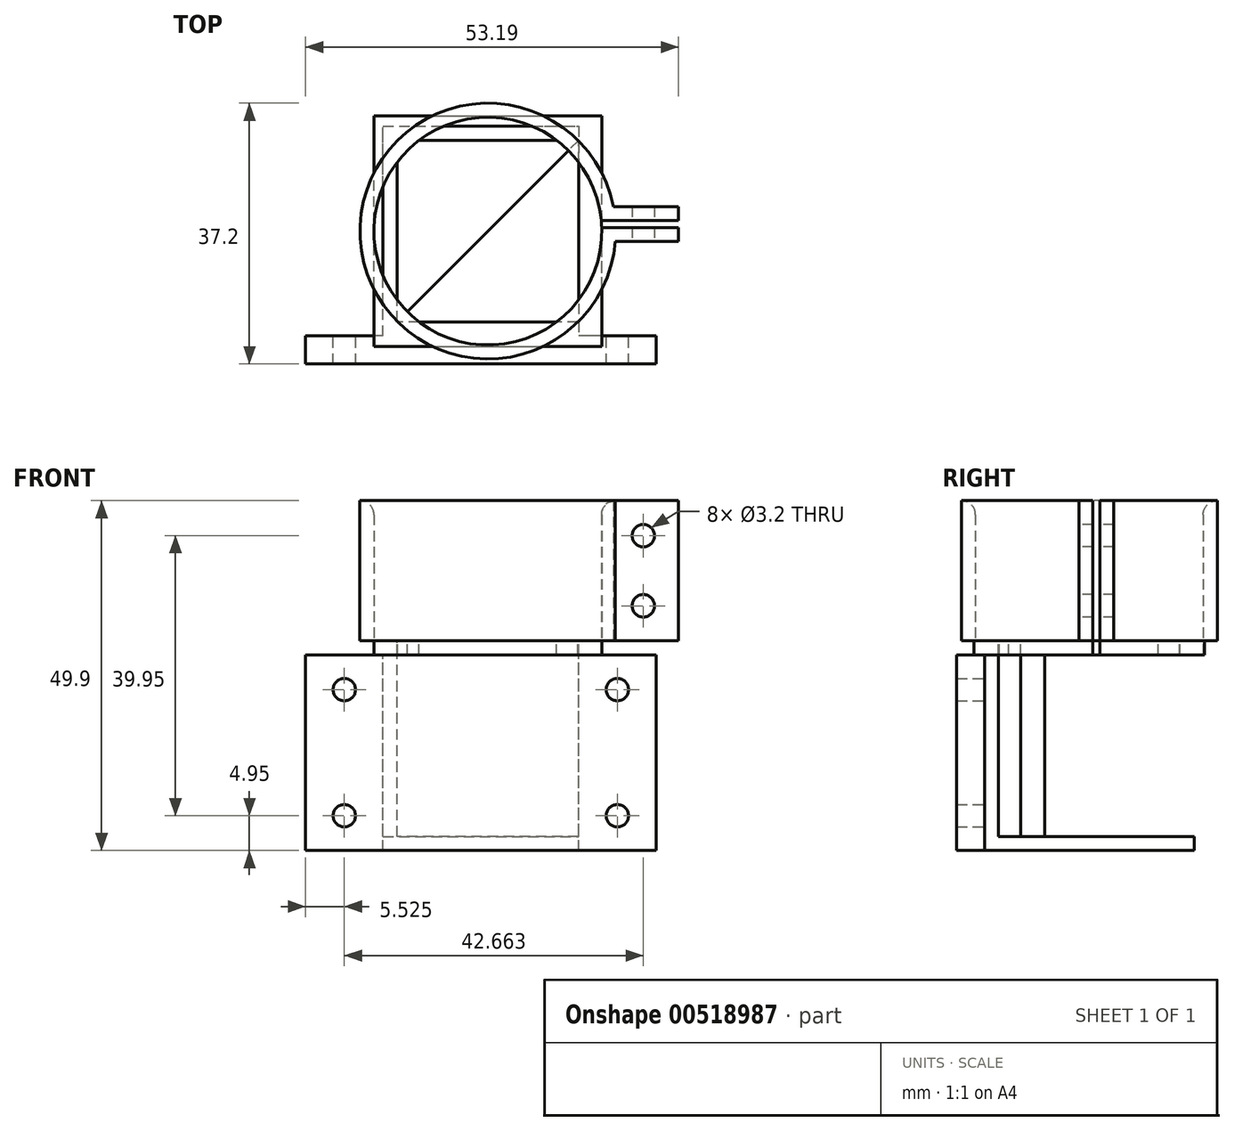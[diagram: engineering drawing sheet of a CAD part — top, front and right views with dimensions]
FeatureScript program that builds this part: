
annotation { "Feature Type Name" : "Feature", "Feature Type Description" : "" }
export const myFeature = defineFeature(function(context is Context, id is Id, definition is map)
    precondition{}
    {
        {
            var Q0;
            Q0=qCreatedBy(makeId("Top.planeOp"),FACE);
            var sketch = newSketch(context, id + "F0", { "sketchPlane" : qUnion([Q0])});
            skCircle(sketch, "E0", {"center": v(0, 0) * mm, "radius": 16.25 * mm});
            skCircle(sketch, "E1", {"center": v(0, 0) * mm, "radius": 18.25 * mm});
            skLineSegment(sketch, "E2", {"start": v(16.18, 1.5) * mm, "end": v(18.19, 1.5) * mm});
            skLineSegment(sketch, "E3", {"start": v(16.24, 0.5) * mm, "end": v(18.19, 0.5) * mm});
            skLineSegment(sketch, "E4", {"start": v(17.91, 3.5) * mm, "end": v(27.19, 3.5) * mm});
            skLineSegment(sketch, "E5", {"start": v(27.19, 3.5) * mm, "end": v(27.19, 1.5) * mm});
            skLineSegment(sketch, "E6", {"start": v(27.19, 1.5) * mm, "end": v(18.19, 1.5) * mm});
            skLineSegment(sketch, "E7", {"start": v(18.19, 0.5) * mm, "end": v(27.19, 0.5) * mm});
            skLineSegment(sketch, "E8", {"start": v(27.19, 0.5) * mm, "end": v(27.19, -1.5) * mm});
            skLineSegment(sketch, "E9", {"start": v(27.19, -1.5) * mm, "end": v(18.19, -1.5) * mm});
            skSolve(sketch);
        }
        {
            var Q0;
            {var subQ0=sQuery(id+"F0.wireOp",EDGE,"E2");Q0=makeQuery(id+"F0.imprint","IMPRINT",FACE,{"disambiguationData":[TD([[makeQuery(id+"F0.imprint","IMPRINT",EDGE,{"derivedFrom":subQ0}),1.0]])]});}
            var Q1;
            {var subQ2=sQuery(id+"F0.wireOp",EDGE,"E4");Q1=makeQuery(id+"F0.imprint","IMPRINT",FACE,{"disambiguationData":[TD([[makeQuery(id+"F0.imprint","IMPRINT",EDGE,{"derivedFrom":subQ2}),-1.0]])]});}
            var Q2;
            {var subQ4=sQuery(id+"F0.wireOp",EDGE,"E8");Q2=makeQuery(id+"F0.imprint","IMPRINT",FACE,{"disambiguationData":[TD([[makeQuery(id+"F0.imprint","IMPRINT",EDGE,{"derivedFrom":subQ4}),-1.0]])]});}
            extrude(context, id + "F1", {"entities" : qUnion([Q0, Q1, Q2]), "depth" : 20 * mm, "offsetDistance" : 25 * mm});
        }
        {
            var Q0;
            Q0=makeQuery(id+"F1.opExtrude","SWEPT_FACE",FACE,{"disambiguationData":[OSD([sQuery(id+"F0.wireOp",EDGE,"E9")])]});
            var sketch = newSketch(context, id + "F2", { "sketchPlane" : qUnion([Q0])});
            skCircle(sketch, "E10", {"center": v(22.19, 15) * mm, "radius": 1.6 * mm});
            skCircle(sketch, "E11", {"center": v(22.19, 5) * mm, "radius": 1.6 * mm});
            skLineSegment(sketch, "E12", {"start": v(22.19, 15) * mm, "end": v(22.19, 20) * mm, "construction": true});
            skLineSegment(sketch, "E13", {"start": v(22.19, 5) * mm, "end": v(22.19, 0) * mm, "construction": true});
            skLineSegment(sketch, "E14", {"start": v(22.19, 15) * mm, "end": v(22.19, 10) * mm, "construction": true});
            skLineSegment(sketch, "E15", {"start": v(22.19, 10) * mm, "end": v(22.19, 5) * mm, "construction": true});
            skLineSegment(sketch, "E16", {"start": v(22.19, 5) * mm, "end": v(27.19, 5) * mm, "construction": true});
            skSolve(sketch);
        }
        {
            var Q0;
            Q0=qSketchRegion(id+"F2",true);
            extrude(context, id + "F3", {"entities" : qUnion([Q0]), "operationType" : NewBodyOperationType.REMOVE, "oppositeDirection" : true, "depth" : 25 * mm, "offsetDistance" : 25 * mm});
        }
        {
            var Q0;
            Q0=makeQuery(id+"F1.opExtrude","CAP_EDGE",EDGE,{"disambiguationData":[OSD([sQuery(id+"F0.wireOp",EDGE,"E0")])],"isStart":false});
            fillet(context, id + "F4", {"entities" : qUnion([Q0]), "radius" : 2 * mm, "tangentPropagation" : true, "allowEdgeOverflow" : false});
        }
        {
            assignVariable(context, id + "F5", {"name" : "PrismSize", "anyValue" : 25.9 * mm});
        }
        {
            var Q0;
            {var subQ5=sQuery(id+"F0.wireOp",EDGE,"E2");Q0=makeQuery(id+"F0.imprint","IMPRINT",FACE,{"disambiguationData":[TD([[makeQuery(id+"F0.imprint","IMPRINT",EDGE,{"derivedFrom":subQ5}),1.0]])]});}
            var sketch = newSketch(context, id + "F6", { "sketchPlane" : qUnion([Q0])});
            skCircle(sketch, "E17", {"center": v(0, 0) * mm, "radius": 16.25 * mm});
            skLineSegment(sketch, "E18.bottom", {"start": v(-12.95, -12.95) * mm, "end": v(12.95, -12.95) * mm});
            skLineSegment(sketch, "E18.top", {"start": v(-12.95, 12.95) * mm, "end": v(12.95, 12.95) * mm});
            skLineSegment(sketch, "E18.left", {"start": v(-12.95, -12.95) * mm, "end": v(-12.95, 12.95) * mm});
            skLineSegment(sketch, "E18.right", {"start": v(12.95, -12.95) * mm, "end": v(12.95, 12.95) * mm});
            skLineSegment(sketch, "E19.bottom", {"start": v(-16.26, -16.45) * mm, "end": v(16.26, -16.45) * mm});
            skLineSegment(sketch, "E19.top", {"start": v(-16.26, 16.45) * mm, "end": v(16.26, 16.45) * mm});
            skLineSegment(sketch, "E19.left", {"start": v(-16.26, -16.45) * mm, "end": v(-16.26, 16.45) * mm});
            skLineSegment(sketch, "E19.right", {"start": v(16.26, -16.45) * mm, "end": v(16.26, 16.45) * mm});
            skLineSegment(sketch, "E20", {"start": v(12.95, 12.95) * mm, "end": v(-12.95, -12.95) * mm});
            skLineSegment(sketch, "E21", {"start": v(12.95, -12.95) * mm, "end": v(-12.95, 12.95) * mm});
            skSolve(sketch);
        }
        {
            var Q0;
            {var subQ0=sQuery(id+"F6.wireOp",EDGE,"E19.left");var subQ1=sQuery(id+"F6.wireOp",EDGE,"E19.bottom");var subQ2=makeQuery(id+"F6.imprint","INTERSECT",VERTEX,{"derivedFrom":[subQ1,subQ0]});Q0=makeQuery(id+"F6.imprint","IMPRINT",FACE,{"disambiguationData":[TD([[makeQuery(id+"F6.imprint","IMPRINT",EDGE,{"disambiguationData":[TD([[subQ2,-1.0]])],"derivedFrom":subQ1}),1.0]])]});}
            var Q1;
            {var subQ6=sQuery(id+"F6.wireOp",EDGE,"E17");var subQ7=makeQuery(id+"F0.imprint","IMPRINT",EDGE,{"derivedFrom":sQuery(id+"F0.wireOp",EDGE,"E2")});var subQ8=makeQuery(id+"F6.imprint","INTERSECT",VERTEX,{"derivedFrom":[subQ7,subQ6]});Q1=makeQuery(id+"F6.imprint","IMPRINT",FACE,{"disambiguationData":[TD([[makeQuery(id+"F6.imprint","IMPRINT",EDGE,{"disambiguationData":[TD([[subQ8,-1.0]])],"derivedFrom":subQ6}),-1.0]])]});}
            var Q2;
            {var subQ0=sQuery(id+"F6.wireOp",EDGE,"E18.top");var subQ1=sQuery(id+"F6.wireOp",EDGE,"E17");var subQ2=makeQuery(id+"F6.imprint","INTERSECT",VERTEX,{"disambiguationData":[OD(0.0)],"derivedFrom":[subQ1,subQ0]});Q2=makeQuery(id+"F6.imprint","IMPRINT",FACE,{"disambiguationData":[TD([[makeQuery(id+"F6.imprint","IMPRINT",EDGE,{"disambiguationData":[TD([[subQ2,-1.0]])],"derivedFrom":subQ1}),1.0]])]});}
            var Q3;
            {var subQ0=sQuery(id+"F6.wireOp",EDGE,"E19.left");var subQ1=sQuery(id+"F6.wireOp",EDGE,"E19.top");var subQ2=makeQuery(id+"F6.imprint","INTERSECT",VERTEX,{"derivedFrom":[subQ1,subQ0]});Q3=makeQuery(id+"F6.imprint","IMPRINT",FACE,{"disambiguationData":[TD([[makeQuery(id+"F6.imprint","IMPRINT",EDGE,{"disambiguationData":[TD([[subQ2,-1.0]])],"derivedFrom":subQ1}),-1.0]])]});}
            var Q4;
            {var subQ0=sQuery(id+"F6.wireOp",EDGE,"E17");var subQ1=makeQuery(id+"F6.imprint","INTERSECT",VERTEX,{"derivedFrom":[makeQuery(id+"F0.imprint","IMPRINT",EDGE,{"derivedFrom":sQuery(id+"F0.wireOp",EDGE,"E2")}),subQ0]});Q4=makeQuery(id+"F6.imprint","IMPRINT",FACE,{"disambiguationData":[TD([[makeQuery(id+"F6.imprint","IMPRINT",EDGE,{"disambiguationData":[TD([[subQ1,1.0]])],"derivedFrom":subQ0}),1.0]])]});}
            var Q5;
            {var subQ0=sQuery(id+"F6.wireOp",EDGE,"E18.left");var subQ1=sQuery(id+"F6.wireOp",EDGE,"E17");var subQ2=makeQuery(id+"F6.imprint","INTERSECT",VERTEX,{"disambiguationData":[OD(0.0)],"derivedFrom":[subQ1,subQ0]});Q5=makeQuery(id+"F6.imprint","IMPRINT",FACE,{"disambiguationData":[TD([[makeQuery(id+"F6.imprint","IMPRINT",EDGE,{"disambiguationData":[TD([[subQ2,-1.0]])],"derivedFrom":subQ1}),1.0]])]});}
            var Q6;
            {var subQ5=sQuery(id+"F6.wireOp",EDGE,"E18.left");var subQ6=sQuery(id+"F6.wireOp",EDGE,"E17");var subQ7=makeQuery(id+"F6.imprint","INTERSECT",VERTEX,{"disambiguationData":[OD(0.0)],"derivedFrom":[subQ6,subQ5]});Q6=makeQuery(id+"F6.imprint","IMPRINT",FACE,{"disambiguationData":[TD([[makeQuery(id+"F6.imprint","IMPRINT",EDGE,{"disambiguationData":[TD([[subQ7,-1.0]])],"derivedFrom":subQ6}),-1.0]])]});}
            var Q7;
            {var subQ0=sQuery(id+"F6.wireOp",EDGE,"E18.bottom");var subQ1=sQuery(id+"F6.wireOp",EDGE,"E17");var subQ9=makeQuery(id+"F6.imprint","INTERSECT",VERTEX,{"disambiguationData":[OD(0.0)],"derivedFrom":[subQ1,subQ0]});Q7=makeQuery(id+"F6.imprint","IMPRINT",FACE,{"disambiguationData":[TD([[makeQuery(id+"F6.imprint","IMPRINT",EDGE,{"disambiguationData":[TD([[subQ9,-1.0]])],"derivedFrom":subQ1}),-1.0]])]});}
            var Q8;
            {var subQ6=sQuery(id+"F6.wireOp",EDGE,"E18.right");var subQ7=sQuery(id+"F6.wireOp",EDGE,"E18.bottom");var subQ8=makeQuery(id+"F6.imprint","INTERSECT",VERTEX,{"derivedFrom":[subQ7,subQ6]});Q8=makeQuery(id+"F6.imprint","IMPRINT",FACE,{"disambiguationData":[TD([[makeQuery(id+"F6.imprint","IMPRINT",EDGE,{"disambiguationData":[TD([[subQ8,1.0]])],"derivedFrom":subQ7}),-1.0]])]});}
            var Q9;
            {var subQ0=sQuery(id+"F6.wireOp",EDGE,"E17");var subQ1=makeQuery(id+"F0.imprint","IMPRINT",EDGE,{"derivedFrom":sQuery(id+"F0.wireOp",EDGE,"E3")});var subQ2=makeQuery(id+"F6.imprint","INTERSECT",VERTEX,{"derivedFrom":[subQ1,subQ0]});Q9=makeQuery(id+"F6.imprint","IMPRINT",FACE,{"disambiguationData":[TD([[makeQuery(id+"F6.imprint","IMPRINT",EDGE,{"disambiguationData":[TD([[subQ2,1.0]])],"derivedFrom":subQ0}),-1.0]])]});}
            var Q10;
            {var subQ0=sQuery(id+"F6.wireOp",EDGE,"E18.bottom");var subQ1=sQuery(id+"F6.wireOp",EDGE,"E17");var subQ2=makeQuery(id+"F6.imprint","INTERSECT",VERTEX,{"disambiguationData":[OD(1.0)],"derivedFrom":[subQ1,subQ0]});Q10=makeQuery(id+"F6.imprint","IMPRINT",FACE,{"disambiguationData":[TD([[makeQuery(id+"F6.imprint","IMPRINT",EDGE,{"disambiguationData":[TD([[subQ2,-1.0]])],"derivedFrom":subQ1}),-1.0]])]});}
            var Q11;
            {var subQ0=sQuery(id+"F6.wireOp",EDGE,"E18.left");var subQ1=sQuery(id+"F6.wireOp",EDGE,"E17");var subQ2=makeQuery(id+"F6.imprint","INTERSECT",VERTEX,{"disambiguationData":[OD(1.0)],"derivedFrom":[subQ1,subQ0]});Q11=makeQuery(id+"F6.imprint","IMPRINT",FACE,{"disambiguationData":[TD([[makeQuery(id+"F6.imprint","IMPRINT",EDGE,{"disambiguationData":[TD([[subQ2,-1.0]])],"derivedFrom":subQ1}),-1.0]])]});}
            var Q12;
            {var subQ7=sQuery(id+"F6.wireOp",EDGE,"E18.right");var subQ8=sQuery(id+"F6.wireOp",EDGE,"E18.top");var subQ9=makeQuery(id+"F6.imprint","INTERSECT",VERTEX,{"derivedFrom":[subQ8,subQ7]});Q12=makeQuery(id+"F6.imprint","IMPRINT",FACE,{"disambiguationData":[TD([[makeQuery(id+"F6.imprint","IMPRINT",EDGE,{"disambiguationData":[TD([[subQ9,1.0]])],"derivedFrom":subQ8}),1.0]])]});}
            var Q13;
            {var subQ5=sQuery(id+"F6.wireOp",EDGE,"E18.top");var subQ6=sQuery(id+"F6.wireOp",EDGE,"E17");var subQ9=makeQuery(id+"F6.imprint","INTERSECT",VERTEX,{"disambiguationData":[OD(0.0)],"derivedFrom":[subQ6,subQ5]});Q13=makeQuery(id+"F6.imprint","IMPRINT",FACE,{"disambiguationData":[TD([[makeQuery(id+"F6.imprint","IMPRINT",EDGE,{"disambiguationData":[TD([[subQ9,-1.0]])],"derivedFrom":subQ6}),-1.0]])]});}
            var Q14;
            {var subQ0=sQuery(id+"F6.wireOp",EDGE,"E18.bottom");var subQ1=sQuery(id+"F6.wireOp",EDGE,"E17");var subQ2=makeQuery(id+"F6.imprint","INTERSECT",VERTEX,{"disambiguationData":[OD(0.0)],"derivedFrom":[subQ1,subQ0]});Q14=makeQuery(id+"F6.imprint","IMPRINT",FACE,{"disambiguationData":[TD([[makeQuery(id+"F6.imprint","IMPRINT",EDGE,{"disambiguationData":[TD([[subQ2,-1.0]])],"derivedFrom":subQ1}),1.0]])]});}
            var Q15;
            {var subQ0=sQuery(id+"F6.wireOp",EDGE,"E19.right");var subQ1=sQuery(id+"F6.wireOp",EDGE,"E19.top");var subQ2=makeQuery(id+"F6.imprint","INTERSECT",VERTEX,{"derivedFrom":[subQ1,subQ0]});Q15=makeQuery(id+"F6.imprint","IMPRINT",FACE,{"disambiguationData":[TD([[makeQuery(id+"F6.imprint","IMPRINT",EDGE,{"disambiguationData":[TD([[subQ2,1.0]])],"derivedFrom":subQ1}),-1.0]])]});}
            var Q16;
            {var subQ0=sQuery(id+"F6.wireOp",EDGE,"E19.right");var subQ1=sQuery(id+"F6.wireOp",EDGE,"E19.bottom");var subQ2=makeQuery(id+"F6.imprint","INTERSECT",VERTEX,{"derivedFrom":[subQ1,subQ0]});Q16=makeQuery(id+"F6.imprint","IMPRINT",FACE,{"disambiguationData":[TD([[makeQuery(id+"F6.imprint","IMPRINT",EDGE,{"disambiguationData":[TD([[subQ2,1.0]])],"derivedFrom":subQ1}),1.0]])]});}
            var Q17;
            {var subQ0=sQuery(id+"F6.wireOp",EDGE,"E20");var subQ1=sQuery(id+"F6.wireOp",EDGE,"E17");var subQ2=makeQuery(id+"F6.imprint","INTERSECT",VERTEX,{"disambiguationData":[OD(1.0)],"derivedFrom":[subQ1,subQ0]});Q17=makeQuery(id+"F6.imprint","IMPRINT",FACE,{"disambiguationData":[TD([[makeQuery(id+"F6.imprint","IMPRINT",EDGE,{"disambiguationData":[TD([[subQ2,-1.0]])],"derivedFrom":subQ1}),-1.0]])]});}
            var Q18;
            {var subQ0=sQuery(id+"F6.wireOp",EDGE,"E21");var subQ1=sQuery(id+"F6.wireOp",EDGE,"E17");var subQ2=makeQuery(id+"F6.imprint","INTERSECT",VERTEX,{"disambiguationData":[OD(1.0)],"derivedFrom":[subQ1,subQ0]});Q18=makeQuery(id+"F6.imprint","IMPRINT",FACE,{"disambiguationData":[TD([[makeQuery(id+"F6.imprint","IMPRINT",EDGE,{"disambiguationData":[TD([[subQ2,-1.0]])],"derivedFrom":subQ1}),-1.0]])]});}
            var Q19;
            {var subQ0=sQuery(id+"F6.wireOp",EDGE,"E18.right");var subQ1=sQuery(id+"F6.wireOp",EDGE,"E17");var subQ2=makeQuery(id+"F6.imprint","INTERSECT",VERTEX,{"disambiguationData":[OD(0.0)],"derivedFrom":[subQ1,subQ0]});Q19=makeQuery(id+"F6.imprint","IMPRINT",FACE,{"disambiguationData":[TD([[makeQuery(id+"F6.imprint","IMPRINT",EDGE,{"disambiguationData":[TD([[subQ2,-1.0]])],"derivedFrom":subQ1}),-1.0]])]});}
            var Q20;
            {var subQ0=sQuery(id+"F6.wireOp",EDGE,"E20");var subQ1=sQuery(id+"F6.wireOp",EDGE,"E17");var subQ2=makeQuery(id+"F6.imprint","INTERSECT",VERTEX,{"disambiguationData":[OD(0.0)],"derivedFrom":[subQ1,subQ0]});Q20=makeQuery(id+"F6.imprint","IMPRINT",FACE,{"disambiguationData":[TD([[makeQuery(id+"F6.imprint","IMPRINT",EDGE,{"disambiguationData":[TD([[subQ2,-1.0]])],"derivedFrom":subQ1}),-1.0]])]});}
            var Q21;
            {var subQ0=sQuery(id+"F6.wireOp",EDGE,"E18.top");var subQ1=sQuery(id+"F6.wireOp",EDGE,"E17");var subQ2=makeQuery(id+"F6.imprint","INTERSECT",VERTEX,{"disambiguationData":[OD(1.0)],"derivedFrom":[subQ1,subQ0]});Q21=makeQuery(id+"F6.imprint","IMPRINT",FACE,{"disambiguationData":[TD([[makeQuery(id+"F6.imprint","IMPRINT",EDGE,{"disambiguationData":[TD([[subQ2,-1.0]])],"derivedFrom":subQ1}),-1.0]])]});}
            var Q22;
            {var subQ0=sQuery(id+"F6.wireOp",EDGE,"E21");var subQ1=sQuery(id+"F6.wireOp",EDGE,"E17");var subQ2=makeQuery(id+"F6.imprint","INTERSECT",VERTEX,{"disambiguationData":[OD(0.0)],"derivedFrom":[subQ1,subQ0]});Q22=makeQuery(id+"F6.imprint","IMPRINT",FACE,{"disambiguationData":[TD([[makeQuery(id+"F6.imprint","IMPRINT",EDGE,{"disambiguationData":[TD([[subQ2,-1.0]])],"derivedFrom":subQ1}),-1.0]])]});}
            extrude(context, id + "F7", {"entities" : qUnion([Q0, Q1, Q2, Q3, Q4, Q5, Q6, Q7, Q8, Q9, Q10, Q11, Q12, Q13, Q14, Q15, Q16, Q17, Q18, Q19, Q20, Q21, Q22]), "operationType" : NewBodyOperationType.ADD, "oppositeDirection" : true, "depth" : 2 * mm, "offsetDistance" : 25 * mm});
        }
        {
            var Q0;
            Q0=makeQuery(id+"F7.opExtrude","CAP_FACE",FACE,{"disambiguationData":[OSD([sQuery(id+"F0.wireOp",EDGE,"E2"),sQuery(id+"F0.wireOp",EDGE,"E3"),sQuery(id+"F6.wireOp",EDGE,"E17"),sQuery(id+"F6.wireOp",EDGE,"E18.bottom"),sQuery(id+"F6.wireOp",EDGE,"E18.top"),sQuery(id+"F6.wireOp",EDGE,"E18.left"),sQuery(id+"F6.wireOp",EDGE,"E18.right"),sQuery(id+"F6.wireOp",EDGE,"E19.bottom"),sQuery(id+"F6.wireOp",EDGE,"E19.top"),sQuery(id+"F6.wireOp",EDGE,"E19.left"),sQuery(id+"F6.wireOp",EDGE,"E19.right")])],"isStart":false});
            var sketch = newSketch(context, id + "F8", { "sketchPlane" : qUnion([Q0])});
            skLineSegment(sketch, "E22.bottom", {"start": v(12.95, 12.95) * mm, "end": v(-12.95, 12.95) * mm});
            skLineSegment(sketch, "E22.top", {"start": v(12.95, -12.95) * mm, "end": v(-12.95, -12.95) * mm});
            skLineSegment(sketch, "E22.left", {"start": v(12.95, 12.95) * mm, "end": v(12.95, -12.95) * mm});
            skLineSegment(sketch, "E22.right", {"start": v(-12.95, 12.95) * mm, "end": v(-12.95, -12.95) * mm});
            skPoint(sketch, "E22.middle", {"position": v(0, 0) * mm});
            skLineSegment(sketch, "E23", {"start": v(12.95, 12.95) * mm, "end": v(12.95, 14.95) * mm});
            skLineSegment(sketch, "E24", {"start": v(12.95, 14.95) * mm, "end": v(-14.95, 14.95) * mm});
            skLineSegment(sketch, "E25", {"start": v(-14.95, 14.95) * mm, "end": v(-14.95, -14.95) * mm});
            skLineSegment(sketch, "E26", {"start": v(-14.95, -14.95) * mm, "end": v(12.95, -14.95) * mm});
            skLineSegment(sketch, "E27", {"start": v(12.95, -14.95) * mm, "end": v(12.95, -12.95) * mm});
            skLineSegment(sketch, "E28", {"start": v(-12.95, -6.35) * mm, "end": v(-14.95, -6.35) * mm, "construction": true});
            skSolve(sketch);
        }
        {
            var Q0;
            {var subQ24=sQuery(id+"F8.wireOp",EDGE,"E23");Q0=makeQuery(id+"F8.imprint","IMPRINT",FACE,{"disambiguationData":[TD([[makeQuery(id+"F8.imprint","IMPRINT",EDGE,{"derivedFrom":subQ24}),1.0]])]});}
            extrude(context, id + "F9", {"entities" : qUnion([Q0]), "operationType" : NewBodyOperationType.ADD, "depth" : getVariable(context, 'PrismSize'), "offsetDistance" : 25 * mm});
        }
        {
            var Q0;
            Q0=makeQuery(id+"F9.opExtrude","CAP_FACE",FACE,{"disambiguationData":[OSD([sQuery(id+"F8.wireOp",EDGE,"E22.bottom"),sQuery(id+"F8.wireOp",EDGE,"E22.top"),sQuery(id+"F8.wireOp",EDGE,"E22.right"),sQuery(id+"F8.wireOp",EDGE,"E23"),sQuery(id+"F8.wireOp",EDGE,"E24"),sQuery(id+"F8.wireOp",EDGE,"E25"),sQuery(id+"F8.wireOp",EDGE,"E26"),sQuery(id+"F8.wireOp",EDGE,"E27")])],"isStart":false});
            var sketch = newSketch(context, id + "F10", { "sketchPlane" : qUnion([Q0])});
            skLineSegment(sketch, "E29.bottom", {"start": v(-14.95, 14.95) * mm, "end": v(12.95, 14.95) * mm});
            skLineSegment(sketch, "E29.top", {"start": v(-14.95, -14.95) * mm, "end": v(12.95, -14.95) * mm});
            skLineSegment(sketch, "E29.left", {"start": v(-14.95, 14.95) * mm, "end": v(-14.95, -14.95) * mm});
            skLineSegment(sketch, "E29.right", {"start": v(12.95, 14.95) * mm, "end": v(12.95, -14.95) * mm});
            skSolve(sketch);
        }
        {
            var Q0;
            Q0 = qSketchRegion(id + "F10", true);
            extrude(context, id + "F11", {"entities" : qUnion([Q0]), "operationType" : NewBodyOperationType.ADD, "depth" : 2 * mm, "offsetDistance" : 25 * mm});
        }
        {
            var Q0;
            Q0=makeQuery(id+"F11.boolean.opBoolean","MERGE",FACE,{"derivedFrom":[makeQuery(id+"F9.opExtrude","SWEPT_FACE",FACE,{"disambiguationData":[OSD([sQuery(id+"F8.wireOp",EDGE,"E24")])]}),makeQuery(id+"F11.opExtrude","SWEPT_FACE",FACE,{"disambiguationData":[OSD([sQuery(id+"F10.wireOp",EDGE,"E29.bottom")])]})]});
            var sketch = newSketch(context, id + "F12", { "sketchPlane" : qUnion([Q0])});
            skLineSegment(sketch, "E30.bottom", {"start": v(-26, -2) * mm, "end": v(24, -2) * mm});
            skLineSegment(sketch, "E30.top", {"start": v(-26, -29.9) * mm, "end": v(24, -29.9) * mm});
            skLineSegment(sketch, "E30.left", {"start": v(-26, -2) * mm, "end": v(-26, -29.9) * mm});
            skLineSegment(sketch, "E30.right", {"start": v(24, -2) * mm, "end": v(24, -29.9) * mm});
            skLineSegment(sketch, "E31", {"start": v(24, -15.95) * mm, "end": v(12.95, -15.95) * mm, "construction": true});
            skLineSegment(sketch, "E32", {"start": v(-14.95, -15.95) * mm, "end": v(-26, -15.95) * mm, "construction": true});
            skCircle(sketch, "E33", {"center": v(-20.48, -6.95) * mm, "radius": 1.6 * mm});
            skCircle(sketch, "E34", {"center": v(-20.48, -24.95) * mm, "radius": 1.6 * mm});
            skCircle(sketch, "E35", {"center": v(18.47, -6.95) * mm, "radius": 1.6 * mm});
            skCircle(sketch, "E36", {"center": v(18.47, -24.95) * mm, "radius": 1.6 * mm});
            skLineSegment(sketch, "E37", {"start": v(-20.48, -6.95) * mm, "end": v(18.47, -6.95) * mm, "construction": true});
            skLineSegment(sketch, "E38", {"start": v(-20.48, -6.95) * mm, "end": v(-20.48, -24.95) * mm, "construction": true});
            skLineSegment(sketch, "E39", {"start": v(-20.48, -24.95) * mm, "end": v(-26, -24.95) * mm, "construction": true});
            skLineSegment(sketch, "E40", {"start": v(-20.48, -24.95) * mm, "end": v(-14.95, -24.95) * mm, "construction": true});
            skLineSegment(sketch, "E41", {"start": v(-20.48, -24.95) * mm, "end": v(-20.48, -29.9) * mm, "construction": true});
            skLineSegment(sketch, "E42", {"start": v(-20.48, -6.95) * mm, "end": v(-20.48, -2) * mm, "construction": true});
            skLineSegment(sketch, "E43", {"start": v(18.47, -24.95) * mm, "end": v(12.95, -24.95) * mm, "construction": true});
            skSolve(sketch);
        }
        {
            var Q0;
            Q0 = qSketchRegion(id + "F12", true);
            extrude(context, id + "F13", {"entities" : qUnion([Q0]), "operationType" : NewBodyOperationType.ADD, "depth" : 4 * mm, "offsetDistance" : 25 * mm});
        }
    });
